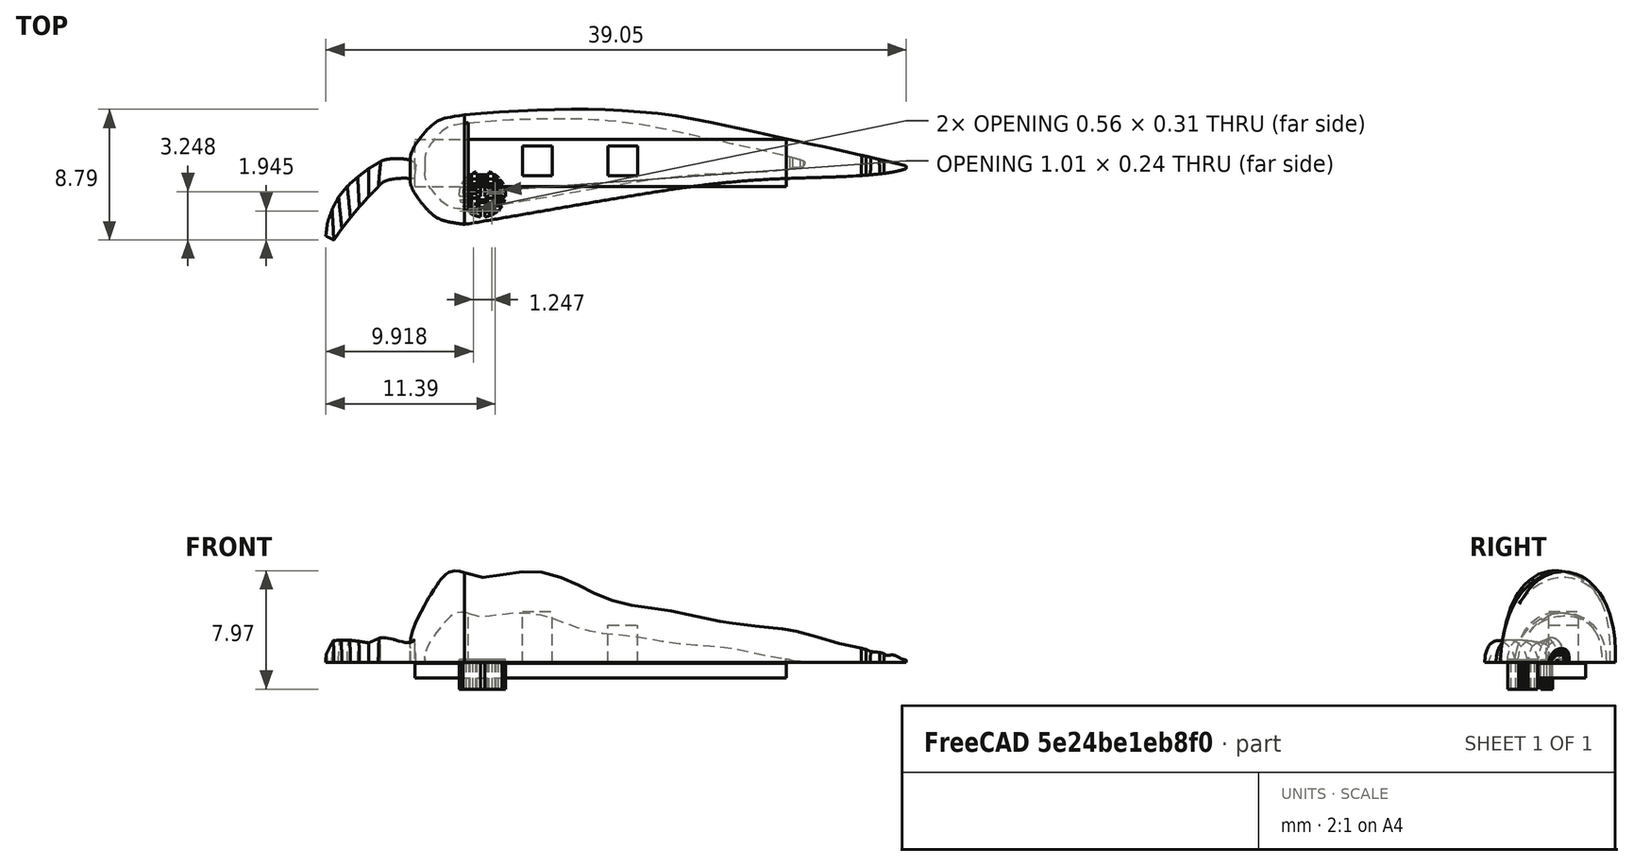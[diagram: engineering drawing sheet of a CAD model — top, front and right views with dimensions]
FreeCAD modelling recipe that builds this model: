
FCSTD DOCUMENT  (FreeCAD 0.19R)
Label: chili_pepper
License: All rights reserved
LicenseURL: http://en.wikipedia.org/wiki/All_rights_reserved
objects: Part::Feature×35, Part::Extrusion×28, Part::FeaturePython×16, Part::Cut×14, Part::Box×4, Sketcher::SketchObject×1
note: 98 computed .brp shape members not serialized (recipe doc carries the construction recipe); baked Part::Feature solids carry a one-line shape summary decoded from their .brp

FEATURE [Part::FeaturePython] Clone001  label="Connect008"  # WARN: FeaturePython — macro-defined, semantics opaque (R4)
  AttacherType = Attacher::AttachEngine3D
  Fuse = false
  Placement = pos=(0.35,0.15,0) rot=(0,0,1;0rad)
  Scale = (0.6,0.6,0.6)
FEATURE [Part::FeaturePython] Clone003  label="Connect010"  # Draft clone (typed FeaturePython)
  AttacherType = Attacher::AttachEngine3D
  Fuse = false
  Objects = -> [Clone001]
  Placement = pos=(0.6,0.35,0.4) rot=(0,0,1;0rad)
  Scale = (0.8,0.8,0.6)
FEATURE [Part::Cut] Cut020
  Base = -> Clone001
  Tool = -> Clone003
FEATURE [Sketcher::SketchObject] Sketch004
  FullyConstrained = false
  sketch-geometry (25):
    g0-g12: Circle x13 (B-spline internal-alignment scaffolding for g13; pole/knot coordinates omitted)
    g13: BSplineCurve PolesCount=13 KnotsCount=11 Degree=3 IsPeriodic=0
    g14-g24: GeomPoint x11 (B-spline internal-alignment scaffolding for g13; pole/knot coordinates omitted)
  constraints (15):
    c: Weight(g0) = 1
    c: Equal(g0,g1)
    c: Equal(g0,g2)
    c: PointOnObject(g2,g1)
    c: Equal(g0, g3-g8) x6
    c: PointOnObject(g8,g6)
    c: Equal(g0,g9)
    c: Equal(g0,g10)
    c: PointOnObject(g10,g9)
    c: Equal(g0,g11)
    c: PointOnObject(g13,g2)
    c: Equal(g0,g12)
    c: Coincident(g12,g0)
    c: InternalAlignment(g0-g12 -> g13) x13
    c: InternalAlignment(g14-g24 -> g13) x11
FEATURE [Part::FeaturePython] Blend_Curve024  # WARN: FeaturePython — macro-defined, semantics opaque (R4)
  AutoScale = false
  Continuity1 = 1
  Continuity2 = 1
  Output = 2
  Parameter1 = 3
  Parameter2 = 2
  Reverse1 = false
  Reverse2 = false
  Scale1 = 3
  Scale2 = -2
FEATURE [Part::FeaturePython] Blend_Curve025  # WARN: FeaturePython — macro-defined, semantics opaque (R4)
  AutoScale = false
  Continuity1 = 1
  Continuity2 = 1
  Output = 2
  Parameter1 = 2.5
  Parameter2 = 1.75
  Reverse1 = false
  Reverse2 = false
  Scale1 = 2.5
  Scale2 = -4
FEATURE [Part::FeaturePython] Blend_Curve026  # WARN: FeaturePython — macro-defined, semantics opaque (R4)
  AutoScale = false
  Continuity1 = 1
  Continuity2 = 1
  Output = 2
  Parameter1 = 2.5
  Parameter2 = 1.75
  Reverse1 = false
  Reverse2 = false
  Scale1 = 3
  Scale2 = -4
FEATURE [Part::FeaturePython] Blend_Curve027  # WARN: FeaturePython — macro-defined, semantics opaque (R4)
  AutoScale = false
  Continuity1 = 1
  Continuity2 = 1
  Output = 2
  Parameter1 = 2.5
  Parameter2 = 1.75
  Reverse1 = false
  Reverse2 = false
  Scale1 = 2.5
  Scale2 = -4
FEATURE [Part::FeaturePython] Blend_Curve028  # WARN: FeaturePython — macro-defined, semantics opaque (R4)
  AutoScale = false
  Continuity1 = 1
  Continuity2 = 1
  Output = 2
  Parameter1 = 2
  Parameter2 = 1.75
  Reverse1 = false
  Reverse2 = false
  Scale1 = 2
  Scale2 = -4
FEATURE [Part::FeaturePython] Blend_Curve030  # WARN: FeaturePython — macro-defined, semantics opaque (R4)
  AutoScale = false
  Continuity1 = 1
  Continuity2 = 1
  Output = 2
  Parameter1 = 2
  Parameter2 = 1.75
  Reverse1 = false
  Reverse2 = false
  Scale1 = 2
  Scale2 = -4
FEATURE [Part::FeaturePython] Blend_Curve031  # WARN: FeaturePython — macro-defined, semantics opaque (R4)
  AutoScale = false
  Continuity1 = 1
  Continuity2 = 1
  Output = 2
  Parameter1 = 2
  Parameter2 = 1.75
  Reverse1 = false
  Reverse2 = false
  Scale1 = 2
  Scale2 = -4
FEATURE [Part::FeaturePython] Blend_Curve034  # WARN: FeaturePython — macro-defined, semantics opaque (R4)
  AutoScale = false
  Continuity1 = 1
  Continuity2 = 1
  Output = 2
  Parameter1 = 2
  Parameter2 = 1.75
  Reverse1 = false
  Reverse2 = false
  Scale1 = 2
  Scale2 = -4
FEATURE [Part::FeaturePython] Blend_Curve036  # WARN: FeaturePython — macro-defined, semantics opaque (R4)
  AutoScale = false
  Continuity1 = 1
  Continuity2 = 1
  Output = 2
  Parameter1 = 2
  Parameter2 = 1.75
  Reverse1 = false
  Reverse2 = false
  Scale1 = 2
  Scale2 = -4
FEATURE [Part::FeaturePython] Blend_Curve037  # WARN: FeaturePython — macro-defined, semantics opaque (R4)
  AutoScale = false
  Continuity1 = 1
  Continuity2 = 1
  Output = 2
  Parameter1 = 2
  Parameter2 = 1.75
  Reverse1 = false
  Reverse2 = false
  Scale1 = 2
  Scale2 = -4
FEATURE [Part::FeaturePython] Blend_Curve038  # WARN: FeaturePython — macro-defined, semantics opaque (R4)
  AutoScale = false
  Continuity1 = 1
  Continuity2 = 1
  Output = 2
  Parameter1 = 2
  Parameter2 = 1.75
  Reverse1 = false
  Reverse2 = false
  Scale1 = 2
  Scale2 = -4
FEATURE [Part::FeaturePython] Blend_Curve048  # WARN: FeaturePython — macro-defined, semantics opaque (R4)
  AutoScale = false
  Continuity1 = 1
  Continuity2 = 1
  Output = 2
  Parameter1 = 2
  Parameter2 = 1.75
  Reverse1 = false
  Reverse2 = false
  Scale1 = 2
  Scale2 = -4
FEATURE [Part::FeaturePython] Blend_Curve049  # WARN: FeaturePython — macro-defined, semantics opaque (R4)
  AutoScale = false
  Continuity1 = 1
  Continuity2 = 1
  Output = 2
  Parameter1 = 2
  Parameter2 = 1.75
  Reverse1 = false
  Reverse2 = false
  Scale1 = 2
  Scale2 = -4
FEATURE [Part::Box] Box014  label="Cube014"
  AttacherType = Attacher::AttachEngine3D
  Height = 15
  Length = 20
  Placement = pos=(-13,-5,-13.2) rot=(0,0,1;0rad)
  Width = 10
FEATURE [Part::Cut] Cut021
  Tool = -> Box014
FEATURE [Part::Box] Box015  label="Cube015"
  AttacherType = Attacher::AttachEngine3D
  Height = 1
  Length = 25
  Placement = pos=(-3,-1,0.75) rot=(0,0,1;0rad)
  Width = 3.2
FEATURE [Part::Box] Box016  label="Cube016"
  AttacherType = Attacher::AttachEngine3D
  Height = 3.45
  Length = 2
  Placement = pos=(4.25,-0.25,1.8) rot=(0,0,1;0rad)
  Width = 2
FEATURE [Part::Box] Box017  label="Cube017"
  AttacherType = Attacher::AttachEngine3D
  Height = 2.5
  Length = 2
  Placement = pos=(10,-0.25,1.8) rot=(0,0,1;0rad)
  Width = 2
FEATURE [Part::Feature] path149
  shape: bbox 2.757 x 0.7854 x 2e-07 mm, 0 faces, 0 solids (baked)
FEATURE [Part::Feature] path149001
  shape: bbox 3.102 x 2.013 x 2e-07 mm, 0 faces, 0 solids (baked)
FEATURE [Part::Feature] path149002
  shape: bbox 1.009 x 0.2448 x 2e-07 mm, 0 faces, 0 solids (baked)
FEATURE [Part::Feature] path149003
  shape: bbox 0.9069 x 0.2004 x 2e-07 mm, 0 faces, 0 solids (baked)
FEATURE [Part::Feature] path149004
  shape: bbox 0.557 x 0.3056 x 2e-07 mm, 0 faces, 0 solids (baked)
FEATURE [Part::Feature] path149005
  shape: bbox 1.009 x 0.2448 x 2e-07 mm, 0 faces, 0 solids (baked)
FEATURE [Part::Feature] path149006
  shape: bbox 0.557 x 0.3056 x 2e-07 mm, 0 faces, 0 solids (baked)
FEATURE [Part::Feature] path2361020
  shape: bbox 0.557 x 0.3056 x 2e-07 mm, 0 faces, 0 solids (baked)
FEATURE [Part::Feature] path2361021
  shape: bbox 1.009 x 0.2448 x 2e-07 mm, 0 faces, 0 solids (baked)
FEATURE [Part::Feature] path2361022
  shape: bbox 0.9069 x 0.2004 x 2e-07 mm, 0 faces, 0 solids (baked)
FEATURE [Part::Feature] path2361023
  shape: bbox 0.557 x 0.3056 x 2e-07 mm, 0 faces, 0 solids (baked)
FEATURE [Part::Extrusion] Extrude081
  Base = -> path2361023
  Dir = (0,0,1)
  DirMode = 0
  FaceMakerClass = Part::FaceMakerBullseye
  LengthFwd = 2
  LengthRev = 0
  Solid = true
  Symmetric = false
FEATURE [Part::Feature] path2361024
  shape: bbox 1.009 x 0.2448 x 2e-07 mm, 0 faces, 0 solids (baked)
FEATURE [Part::Extrusion] Extrude080
  Base = -> path2361024
  Dir = (0,0,1)
  DirMode = 0
  FaceMakerClass = Part::FaceMakerBullseye
  LengthFwd = 2
  LengthRev = 0
  Solid = true
  Symmetric = false
FEATURE [Part::Extrusion] Extrude082
  Base = -> path2361022
  Dir = (0,0,1)
  DirMode = 0
  FaceMakerClass = Part::FaceMakerBullseye
  LengthFwd = 2
  LengthRev = 0
  Solid = true
  Symmetric = false
FEATURE [Part::Feature] path2361025
  shape: bbox 3.102 x 2.013 x 2e-07 mm, 0 faces, 0 solids (baked)
FEATURE [Part::Extrusion] Extrude079
  Base = -> path2361025
  Dir = (0,0,1)
  DirMode = 0
  FaceMakerClass = Part::FaceMakerBullseye
  LengthFwd = 2
  LengthRev = 0
  Solid = true
  Symmetric = false
FEATURE [Part::Feature] path2361026
  shape: bbox 2.757 x 0.7854 x 2e-07 mm, 0 faces, 0 solids (baked)
FEATURE [Part::Extrusion] Extrude078
  Base = -> path2361026
  Dir = (0,0,1)
  DirMode = 0
  FaceMakerClass = Part::FaceMakerBullseye
  LengthFwd = 2
  LengthRev = 0
  Solid = true
  Symmetric = false
FEATURE [Part::Extrusion] Extrude083
  Base = -> path2361021
  Dir = (0,0,1)
  DirMode = 0
  FaceMakerClass = Part::FaceMakerBullseye
  LengthFwd = 2
  LengthRev = 0
  Solid = true
  Symmetric = false
FEATURE [Part::Extrusion] Extrude084
  Base = -> path2361020
  Dir = (0,0,1)
  DirMode = 0
  FaceMakerClass = Part::FaceMakerBullseye
  LengthFwd = 2
  LengthRev = 0
  Solid = true
  Symmetric = false
FEATURE [Part::Cut] Cut028
  Base = -> Extrude079
  Tool = -> Extrude081
FEATURE [Part::Cut] Cut027
  Base = -> Cut028
  Tool = -> Extrude084
FEATURE [Part::Cut] Cut030
  Base = -> Cut027
  Tool = -> Extrude080
FEATURE [Part::Feature] path2361027
  shape: bbox 3.102 x 2.013 x 2e-07 mm, 0 faces, 0 solids (baked)
FEATURE [Part::Feature] path2361028
  shape: bbox 1.009 x 0.2448 x 2e-07 mm, 0 faces, 0 solids (baked)
FEATURE [Part::Feature] path2361029
  shape: bbox 2.757 x 0.7854 x 2e-07 mm, 0 faces, 0 solids (baked)
FEATURE [Part::Feature] path2361030
  shape: bbox 0.557 x 0.3056 x 2e-07 mm, 0 faces, 0 solids (baked)
FEATURE [Part::Extrusion] Extrude086
  Base = -> path2361028
  Dir = (0,0,1)
  DirMode = 0
  FaceMakerClass = Part::FaceMakerBullseye
  LengthFwd = 2
  LengthRev = 0
  Solid = true
  Symmetric = false
FEATURE [Part::Extrusion] Extrude089
  Base = -> path2361029
  Dir = (0,0,1)
  DirMode = 0
  FaceMakerClass = Part::FaceMakerBullseye
  LengthFwd = 2
  LengthRev = 0
  Solid = true
  Symmetric = false
FEATURE [Part::Extrusion] Extrude090
  Base = -> path2361030
  Dir = (0,0,1)
  DirMode = 0
  FaceMakerClass = Part::FaceMakerBullseye
  LengthFwd = 2
  LengthRev = 0
  Solid = true
  Symmetric = false
FEATURE [Part::Feature] path2361031
  shape: bbox 0.9069 x 0.2004 x 2e-07 mm, 0 faces, 0 solids (baked)
FEATURE [Part::Extrusion] Extrude085
  Base = -> path2361031
  Dir = (0,0,1)
  DirMode = 0
  FaceMakerClass = Part::FaceMakerBullseye
  LengthFwd = 2
  LengthRev = 0
  Solid = true
  Symmetric = false
FEATURE [Part::Feature] path2361032
  shape: bbox 1.009 x 0.2448 x 2e-07 mm, 0 faces, 0 solids (baked)
FEATURE [Part::Extrusion] Extrude088
  Base = -> path2361032
  Dir = (0,0,1)
  DirMode = 0
  FaceMakerClass = Part::FaceMakerBullseye
  LengthFwd = 2
  LengthRev = 0
  Solid = true
  Symmetric = false
FEATURE [Part::Extrusion] Extrude091
  Base = -> path2361027
  Dir = (0,0,1)
  DirMode = 0
  FaceMakerClass = Part::FaceMakerBullseye
  LengthFwd = 2
  LengthRev = 0
  Solid = true
  Symmetric = false
FEATURE [Part::Feature] path2361033
  shape: bbox 0.557 x 0.3056 x 2e-07 mm, 0 faces, 0 solids (baked)
FEATURE [Part::Extrusion] Extrude087
  Base = -> path2361033
  Dir = (0,0,1)
  DirMode = 0
  FaceMakerClass = Part::FaceMakerBullseye
  LengthFwd = 2
  LengthRev = 0
  Solid = true
  Symmetric = false
FEATURE [Part::Cut] Cut036
  Base = -> Extrude091
  Tool = -> Extrude087
FEATURE [Part::Cut] Cut033
  Base = -> Cut036
  Tool = -> Extrude090
FEATURE [Part::Cut] Cut035
  Base = -> Cut033
  Tool = -> Extrude086
FEATURE [Part::Feature] path2361034
  shape: bbox 0.557 x 0.3056 x 2e-07 mm, 0 faces, 0 solids (baked)
FEATURE [Part::Feature] path2361035
  shape: bbox 2.757 x 0.7854 x 2e-07 mm, 0 faces, 0 solids (baked)
FEATURE [Part::Feature] path2361036
  shape: bbox 0.9069 x 0.2004 x 2e-07 mm, 0 faces, 0 solids (baked)
FEATURE [Part::Extrusion] Extrude093
  Base = -> path2361036
  Dir = (0,0,1)
  DirMode = 0
  FaceMakerClass = Part::FaceMakerBullseye
  LengthFwd = 2
  LengthRev = 0
  Solid = true
  Symmetric = false
FEATURE [Part::Feature] path2361037
  shape: bbox 1.009 x 0.2448 x 2e-07 mm, 0 faces, 0 solids (baked)
FEATURE [Part::Extrusion] Extrude092
  Base = -> path2361037
  Dir = (0,0,1)
  DirMode = 0
  FaceMakerClass = Part::FaceMakerBullseye
  LengthFwd = 2
  LengthRev = 0
  Solid = true
  Symmetric = false
FEATURE [Part::Feature] path2361038
  shape: bbox 1.009 x 0.2448 x 2e-07 mm, 0 faces, 0 solids (baked)
FEATURE [Part::Extrusion] Extrude095
  Base = -> path2361038
  Dir = (0,0,1)
  DirMode = 0
  FaceMakerClass = Part::FaceMakerBullseye
  LengthFwd = 2
  LengthRev = 0
  Solid = true
  Symmetric = false
FEATURE [Part::Extrusion] Extrude096
  Base = -> path2361034
  Dir = (0,0,1)
  DirMode = 0
  FaceMakerClass = Part::FaceMakerBullseye
  LengthFwd = 2
  LengthRev = 0
  Solid = true
  Symmetric = false
FEATURE [Part::Feature] path2361039
  shape: bbox 0.557 x 0.3056 x 2e-07 mm, 0 faces, 0 solids (baked)
FEATURE [Part::Feature] path2361040
  shape: bbox 3.102 x 2.013 x 2e-07 mm, 0 faces, 0 solids (baked)
FEATURE [Part::Extrusion] Extrude094
  Base = -> path2361040
  Dir = (0,0,1)
  DirMode = 0
  FaceMakerClass = Part::FaceMakerBullseye
  LengthFwd = 2
  LengthRev = 0
  Solid = true
  Symmetric = false
FEATURE [Part::Extrusion] Extrude097
  Base = -> path2361035
  Dir = (0,0,1)
  DirMode = 0
  FaceMakerClass = Part::FaceMakerBullseye
  LengthFwd = 2
  LengthRev = 0
  Solid = true
  Symmetric = false
FEATURE [Part::Extrusion] Extrude098
  Base = -> path2361039
  Dir = (0,0,1)
  DirMode = 0
  FaceMakerClass = Part::FaceMakerBullseye
  LengthFwd = 2
  LengthRev = 0
  Solid = true
  Symmetric = false
FEATURE [Part::Cut] Cut041
  Base = -> Extrude094
  Tool = -> Extrude098
FEATURE [Part::Cut] Cut038
  Base = -> Cut041
  Tool = -> Extrude096
FEATURE [Part::Cut] Cut040
  Base = -> Cut038
  Tool = -> Extrude095
FEATURE [Part::Feature] path2361041
  shape: bbox 0.557 x 0.3056 x 2e-07 mm, 0 faces, 0 solids (baked)
FEATURE [Part::Feature] path2361042
  shape: bbox 1.009 x 0.2448 x 2e-07 mm, 0 faces, 0 solids (baked)
FEATURE [Part::Feature] path2361043
  shape: bbox 0.9069 x 0.2004 x 2e-07 mm, 0 faces, 0 solids (baked)
FEATURE [Part::Feature] path2361044
  shape: bbox 0.557 x 0.3056 x 2e-07 mm, 0 faces, 0 solids (baked)
FEATURE [Part::Extrusion] Extrude102
  Base = -> path2361044
  Dir = (0,0,1)
  DirMode = 0
  FaceMakerClass = Part::FaceMakerBullseye
  LengthFwd = 2
  LengthRev = 0
  Solid = true
  Symmetric = false
FEATURE [Part::Feature] path2361045
  shape: bbox 1.009 x 0.2448 x 2e-07 mm, 0 faces, 0 solids (baked)
FEATURE [Part::Extrusion] Extrude101
  Base = -> path2361045
  Dir = (0,0,1)
  DirMode = 0
  FaceMakerClass = Part::FaceMakerBullseye
  LengthFwd = 2
  LengthRev = 0
  Solid = true
  Symmetric = false
FEATURE [Part::Extrusion] Extrude103
  Base = -> path2361043
  Dir = (0,0,1)
  DirMode = 0
  FaceMakerClass = Part::FaceMakerBullseye
  LengthFwd = 2
  LengthRev = 0
  Solid = true
  Symmetric = false
FEATURE [Part::Feature] path2361046
  shape: bbox 3.102 x 2.013 x 2e-07 mm, 0 faces, 0 solids (baked)
FEATURE [Part::Extrusion] Extrude100
  Base = -> path2361046
  Dir = (0,0,1)
  DirMode = 0
  FaceMakerClass = Part::FaceMakerBullseye
  LengthFwd = 2
  LengthRev = 0
  Solid = true
  Symmetric = false
FEATURE [Part::Feature] path2361047
  shape: bbox 2.757 x 0.7854 x 2e-07 mm, 0 faces, 0 solids (baked)
FEATURE [Part::Extrusion] Extrude099
  Base = -> path2361047
  Dir = (0,0,1)
  DirMode = 0
  FaceMakerClass = Part::FaceMakerBullseye
  LengthFwd = 2
  LengthRev = 0
  Solid = true
  Symmetric = false
FEATURE [Part::Extrusion] Extrude104
  Base = -> path2361042
  Dir = (0,0,1)
  DirMode = 0
  FaceMakerClass = Part::FaceMakerBullseye
  LengthFwd = 2
  LengthRev = 0
  Solid = true
  Symmetric = false
FEATURE [Part::Extrusion] Extrude105
  Base = -> path2361041
  Dir = (0,0,1)
  DirMode = 0
  FaceMakerClass = Part::FaceMakerBullseye
  LengthFwd = 2
  LengthRev = 0
  Solid = true
  Symmetric = false
FEATURE [Part::Cut] Cut043
  Base = -> Extrude100
  Tool = -> Extrude102
FEATURE [Part::Cut] Cut042
  Base = -> Cut043
  Tool = -> Extrude105
FEATURE [Part::Cut] Cut045
  Base = -> Cut042
  Tool = -> Extrude101
FEATURE [Part::FeaturePython] Discretized_Edge008  # WARN: FeaturePython — macro-defined, semantics opaque (R4)
  Algorithm = 0
  Angular = 0.1
  Curvature = 0.1
  Deflection = 1
  Distance = 1
  Edge = -> Sketch004 [Edge1]
  Minimum = 2
  NormalizedParameters = [0,0.0234858,0.104232,0.173762,0.226018,0.267882,0.308028,0.350567,0.392726,0.431184,0.470141,0.522032,0.642905,0.695035,0.725701,0.75198,0.778661,0.811486,0.864224,0.918817,1]
  Number = 20
  ParameterFirst = 0
  ParameterLast = 1
  Points = (20) [(-3.24184,-0.453891,0),(-3.13973,0.475104,0),(-3.67102,0.823641,0),(-4.60035,0.89888,0),(-5.50336,0.697618,0),(-6.30568,0.21977,0),+14 more]
  Target = 0
